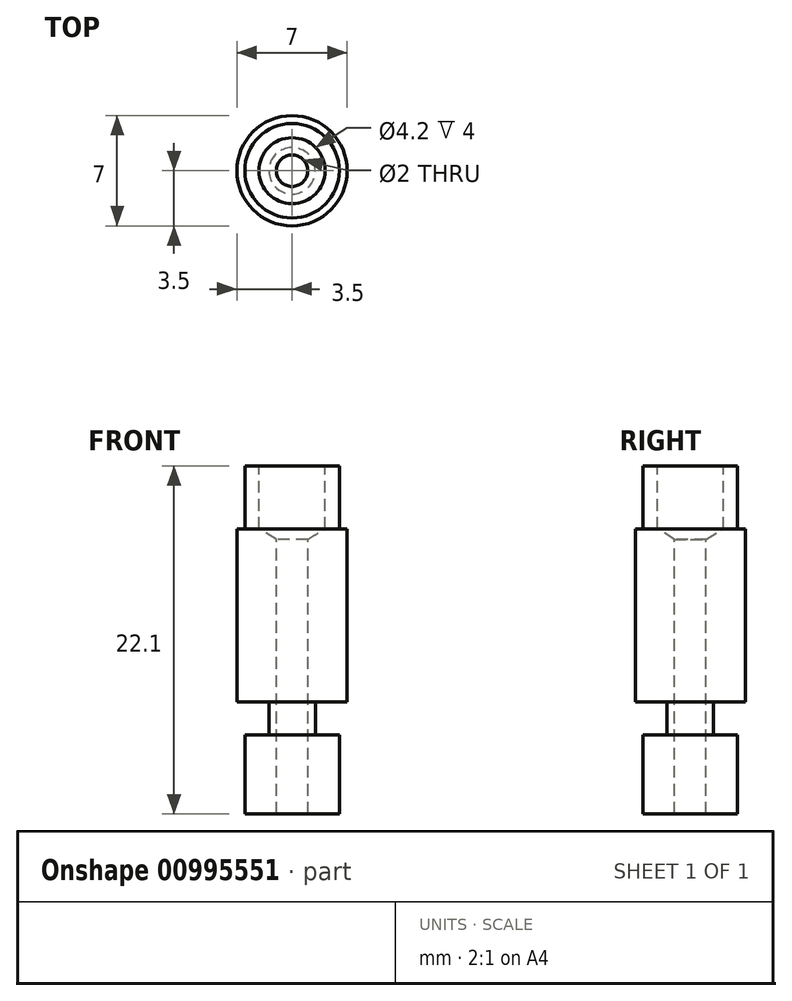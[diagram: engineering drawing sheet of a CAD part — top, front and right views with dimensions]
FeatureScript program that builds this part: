
annotation { "Feature Type Name" : "Feature", "Feature Type Description" : "" }
export const myFeature = defineFeature(function(context is Context, id is Id, definition is map)
    precondition{}
    {
        {
            var Q0;
            Q0=qCreatedBy(makeId("Front.planeOp"),FACE);
            var sketch = newSketch(context, id + "F0", { "sketchPlane" : qUnion([Q0])});
            skLineSegment(sketch, "E0", {"start": v(2.1, 2.36) * mm, "end": v(2.1, 6.36) * mm});
            skLineSegment(sketch, "E1", {"start": v(2.1, 6.36) * mm, "end": v(3, 6.36) * mm});
            skLineSegment(sketch, "E2", {"start": v(3, 6.36) * mm, "end": v(3, 2.36) * mm});
            skLineSegment(sketch, "E3", {"start": v(3, 2.36) * mm, "end": v(3.5, 2.36) * mm});
            skLineSegment(sketch, "E4", {"start": v(3.5, 2.36) * mm, "end": v(3.5, -8.64) * mm});
            skLineSegment(sketch, "E5", {"start": v(3.5, -8.64) * mm, "end": v(1.48, -8.64) * mm});
            skLineSegment(sketch, "E6", {"start": v(1.48, -8.64) * mm, "end": v(1.48, -10.74) * mm});
            skLineSegment(sketch, "E7", {"start": v(1.48, -10.74) * mm, "end": v(3, -10.74) * mm});
            skLineSegment(sketch, "E8", {"start": v(3, -10.74) * mm, "end": v(3, -15.74) * mm});
            skLineSegment(sketch, "E9", {"start": v(3, -15.74) * mm, "end": v(1, -15.74) * mm});
            skLineSegment(sketch, "E10", {"start": v(1, -15.74) * mm, "end": v(1, 1.7) * mm});
            skLineSegment(sketch, "E11", {"start": v(1, 1.7) * mm, "end": v(2.1, 2.36) * mm});
            skLineSegment(sketch, "E12", {"start": v(0, 7.45) * mm, "end": v(0, -13.16) * mm, "construction": true});
            skSolve(sketch);
        }
        {
            var Q0;
            Q0=makeQuery(id+"F0.imprint","IMPRINT",FACE,{"disambiguationData":[TD([[makeQuery(id+"F0.imprint","IMPRINT",EDGE,{"derivedFrom":sQuery(id+"F0.wireOp",EDGE,"E0")}),-1.0]])]});
            var Q1;
            Q1=sQuery(id+"F0.wireOp",EDGE,"E12");
            revolve(context, id + "F1", {"surfaceOperationType" : NewSurfaceOperationType.NEW, "entities" : qUnion([Q0]), "axis" : qUnion([Q1]), "revolveType" : RevolveType.FULL});
        }
    });
